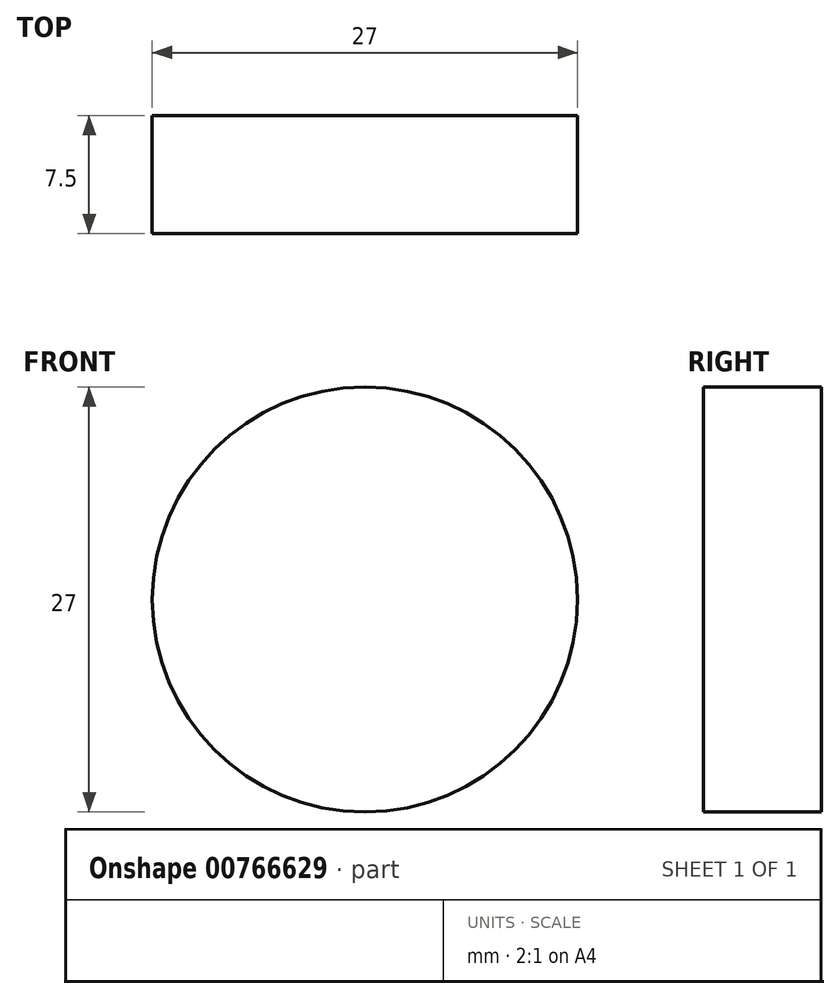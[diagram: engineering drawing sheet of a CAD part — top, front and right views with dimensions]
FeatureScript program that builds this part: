
annotation { "Feature Type Name" : "Feature", "Feature Type Description" : "" }
export const myFeature = defineFeature(function(context is Context, id is Id, definition is map)
    precondition{}
    {
        {
            var Q0;
            Q0=qCreatedBy(makeId("Front.planeOp"),FACE);
            var sketch = newSketch(context, id + "F0", { "sketchPlane" : qUnion([Q0])});
            skCircle(sketch, "E0", {"center": v(0, 0) * mm, "radius": 13.5 * mm});
            skSolve(sketch);
        }
        {
            var Q0;
            Q0=makeQuery(id+"F0.imprint","IMPRINT",FACE,{"disambiguationData":[TD([[makeQuery(id+"F0.imprint","IMPRINT",EDGE,{"derivedFrom":sQuery(id+"F0.wireOp",EDGE,"E0")}),1.0]])]});
            extrude(context, id + "F1", {"entities" : qUnion([Q0]), "depth" : 7.5 * mm, "offsetDistance" : 25 * mm});
        }
    });
